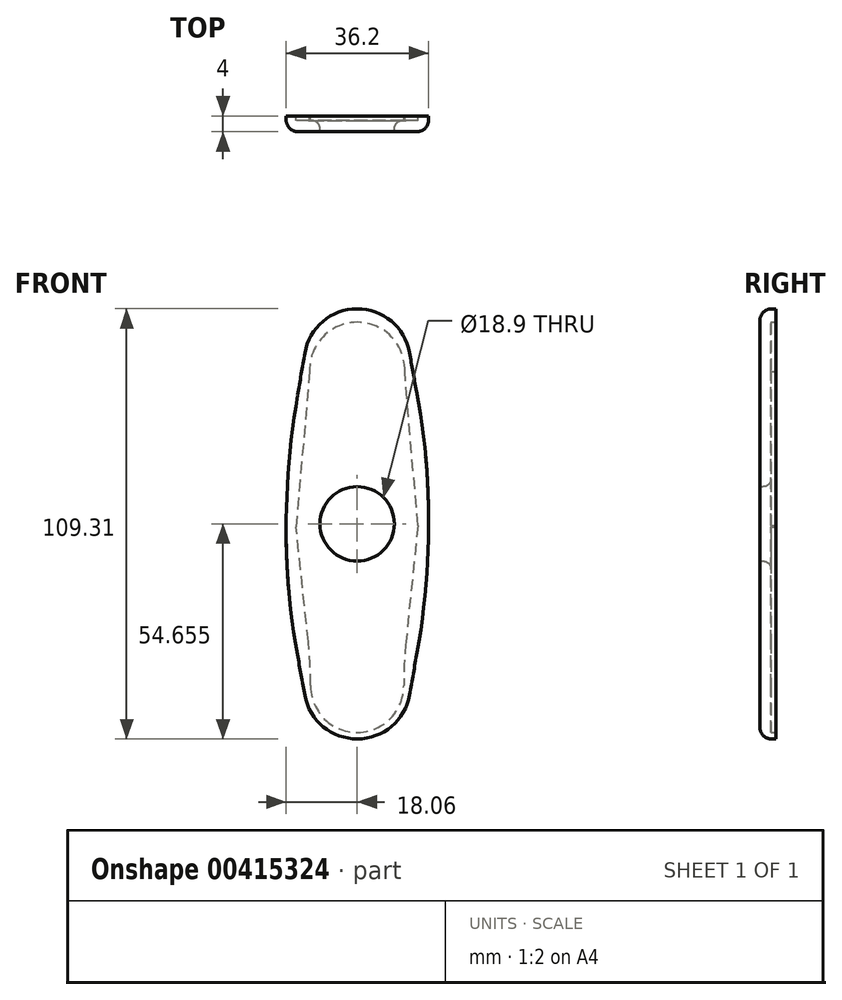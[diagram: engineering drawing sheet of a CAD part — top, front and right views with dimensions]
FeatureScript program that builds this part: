
annotation { "Feature Type Name" : "Feature", "Feature Type Description" : "" }
export const myFeature = defineFeature(function(context is Context, id is Id, definition is map)
    precondition{}
    {
        {
            var Q0;
            Q0=qCreatedBy(makeId("Front.planeOp"),FACE);
            var sketch = newSketch(context, id + "F0", { "sketchPlane" : qUnion([Q0])});
            skCircle(sketch, "E0", {"center": v(0, 60.15) * mm, "radius": 13.5 * mm});
            skCircle(sketch, "E1", {"center": v(0, -22.16) * mm, "radius": 13.5 * mm});
            skFitSpline(sketch, "E2", {"points": [v(13.5, 60.15) * mm, v(13.5, -22.16) * mm], "startDerivative": vector(18.92, -80.32) * mm, "endDerivative": vector(-18.2, -80.32) * mm});
            skFitSpline(sketch, "E3", {"points": [v(-13.5, 60.15) * mm, v(-13.5, -22.18) * mm], "startDerivative": vector(-17.3, -80.42) * mm, "endDerivative": vector(19.13, -79.67) * mm});
            skCircle(sketch, "E4", {"center": v(0, 19) * mm, "radius": 9.45 * mm});
            skCircle(sketch, "E5", {"center": v(0, 19) * mm, "radius": 11 * mm});
            skSolve(sketch);
        }
        {
            var Q0;
            Q0 = qSketchRegion(id + "F0", true);
            extrude(context, id + "F1", {"entities" : qUnion([Q0]), "depth" : 3 * mm});
        }
        {
            var Q0;
            Q0=makeQuery(id+"F1.opExtrude","SWEPT_EDGE",EDGE,{"disambiguationData":[OSD([sQuery(id+"F0.wireOp",EDGE,"E0"),sQuery(id+"F0.wireOp",EDGE,"E2")])]});
            fillet(context, id + "F2", {"entities" : qUnion([Q0]), "radius" : 802.32 * mm, "tangentPropagation" : true, "allowEdgeOverflow" : false});
        }
        {
            var Q0;
            Q0=makeQuery(id+"F1.opExtrude","SWEPT_EDGE",EDGE,{"disambiguationData":[OSD([sQuery(id+"F0.wireOp",EDGE,"E0"),sQuery(id+"F0.wireOp",EDGE,"E3")])]});
            fillet(context, id + "F3", {"entities" : qUnion([Q0]), "radius" : 4378.56 * mm, "tangentPropagation" : true, "allowEdgeOverflow" : false});
        }
        {
            var Q0;
            Q0=makeQuery(id+"F1.opExtrude","SWEPT_EDGE",EDGE,{"disambiguationData":[OSD([sQuery(id+"F0.wireOp",EDGE,"E1"),sQuery(id+"F0.wireOp",EDGE,"E2")])]});
            fillet(context, id + "F4", {"entities" : qUnion([Q0]), "radius" : 6629.57 * mm, "tangentPropagation" : true, "allowEdgeOverflow" : false});
        }
        {
            var Q0;
            Q0=makeQuery(id+"F1.opExtrude","SWEPT_EDGE",EDGE,{"disambiguationData":[OSD([sQuery(id+"F0.wireOp",EDGE,"E1"),sQuery(id+"F0.wireOp",EDGE,"E3")])]});
            fillet(context, id + "F5", {"entities" : qUnion([Q0]), "radius" : 5921.06 * mm, "tangentPropagation" : true, "allowEdgeOverflow" : false});
        }
        {
            var Q0;
            Q0=makeQuery(id+"F0.imprint","IMPRINT",FACE,{"disambiguationData":[TD([[makeQuery(id+"F0.imprint","IMPRINT",EDGE,{"derivedFrom":sQuery(id+"F0.wireOp",EDGE,"E4")}),-1.0]])]});
            extrude(context, id + "F6", {"entities" : qUnion([Q0]), "operationType" : NewBodyOperationType.ADD, "depth" : 4 * mm});
        }
        {
            var Q0;
            Q0=makeQuery(id+"F1.opExtrude","CAP_FACE",FACE,{"disambiguationData":[OSD([sQuery(id+"F0.wireOp",EDGE,"E0"),sQuery(id+"F0.wireOp",EDGE,"E1"),sQuery(id+"F0.wireOp",EDGE,"E2"),sQuery(id+"F0.wireOp",EDGE,"E3"),sQuery(id+"F0.wireOp",EDGE,"E5")])],"isStart":false});
            extrude(context, id + "F7", {"entities" : qUnion([Q0]), "operationType" : NewBodyOperationType.ADD, "depth" : 1 * mm});
        }
        {
            var Q0;
            {var subQ0=sQuery(id+"F0.wireOp",EDGE,"E5");Q0=makeQuery(id+"F6.boolean.opBoolean","MERGE",FACE,{"derivedFrom":[makeQuery(id+"F1.opExtrude","CAP_FACE",FACE,{"disambiguationData":[OSD([sQuery(id+"F0.wireOp",EDGE,"E0"),sQuery(id+"F0.wireOp",EDGE,"E1"),sQuery(id+"F0.wireOp",EDGE,"E2"),sQuery(id+"F0.wireOp",EDGE,"E3"),subQ0])],"isStart":true}),makeQuery(id+"F6.opExtrude","CAP_FACE",FACE,{"disambiguationData":[OSD([sQuery(id+"F0.wireOp",EDGE,"E4"),subQ0])],"isStart":true})]});}
            var sketch = newSketch(context, id + "F8", { "sketchPlane" : qUnion([Q0])});
            skCircle(sketch, "E6", {"center": v(0, -22.16) * mm, "radius": 11.84 * mm});
            skPoint(sketch, "E7.centerSnap0", {"position": v(0.04, 73.64) * mm});
            skLineSegment(sketch, "E8", {"start": v(11.5, -19.38) * mm, "end": v(15.54, 18.27) * mm});
            skPoint(sketch, "E8.startSnap0", {"position": v(14.24, -19.38) * mm});
            skLineSegment(sketch, "E9", {"start": v(-15.41, 18.63) * mm, "end": v(-11.5, -19.38) * mm});
            skCircle(sketch, "E10", {"center": v(0, 58.13) * mm, "radius": 12.1 * mm});
            skLineSegment(sketch, "E11", {"start": v(-15.41, 18.63) * mm, "end": v(-11.84, 60.64) * mm});
            skLineSegment(sketch, "E12", {"start": v(11.84, 60.64) * mm, "end": v(15.54, 18.27) * mm});
            skSolve(sketch);
        }
        {
            var Q0;
            Q0 = qSketchRegion(id + "F8", true);
            extrude(context, id + "F9", {"entities" : qUnion([Q0]), "operationType" : NewBodyOperationType.REMOVE, "oppositeDirection" : true, "depth" : 1.2 * mm});
        }
        {
            var Q0;
            {var subQ0=sQuery(id+"F0.wireOp",EDGE,"E5");var subQ1=sQuery(id+"F0.wireOp",EDGE,"E3");var subQ2=sQuery(id+"F0.wireOp",EDGE,"E2");var subQ3=sQuery(id+"F0.wireOp",EDGE,"E1");var subQ4=sQuery(id+"F0.wireOp",EDGE,"E0");Q0=makeQuery(id+"F7.opExtrude","CAP_EDGE",EDGE,{"disambiguationData":[OSD([subQ4,subQ3,subQ2,subQ1,subQ0]),TDD([makeQuery(id+"F2.opFillet","BLEND_EDGE",EDGE,{"blendedFrom":[makeQuery(id+"F1.opExtrude","SWEPT_EDGE",EDGE,{"disambiguationData":[OSD([subQ4,subQ2])]}),makeQuery(id+"F1.opExtrude","CAP_FACE",FACE,{"disambiguationData":[OSD([subQ4,subQ3,subQ2,subQ1,subQ0])],"isStart":false})],"blendedInto":[makeQuery(id+"F1.opExtrude","CAP_FACE",FACE,{"disambiguationData":[OSD([subQ4,subQ3,subQ2,subQ1,subQ0])],"isStart":false})]})])],"isStart":false});}
            var Q1;
            Q1=makeQuery(id+"F7.opExtrude","CAP_EDGE",EDGE,{"disambiguationData":[OSD([sQuery(id+"F0.wireOp",EDGE,"E0")])],"isStart":false});
            var Q2;
            Q2=makeQuery(id+"F7.opExtrude","CAP_EDGE",EDGE,{"disambiguationData":[OSD([sQuery(id+"F0.wireOp",EDGE,"E2")])],"isStart":false});
            var Q3;
            {var subQ0=sQuery(id+"F0.wireOp",EDGE,"E5");var subQ1=sQuery(id+"F0.wireOp",EDGE,"E3");var subQ2=sQuery(id+"F0.wireOp",EDGE,"E2");var subQ3=sQuery(id+"F0.wireOp",EDGE,"E1");var subQ4=sQuery(id+"F0.wireOp",EDGE,"E0");Q3=makeQuery(id+"F7.opExtrude","CAP_EDGE",EDGE,{"disambiguationData":[OSD([subQ4,subQ3,subQ2,subQ1,subQ0]),TDD([makeQuery(id+"F3.opFillet","BLEND_EDGE",EDGE,{"blendedFrom":[makeQuery(id+"F1.opExtrude","SWEPT_EDGE",EDGE,{"disambiguationData":[OSD([subQ4,subQ1])]}),makeQuery(id+"F1.opExtrude","CAP_FACE",FACE,{"disambiguationData":[OSD([subQ4,subQ3,subQ2,subQ1,subQ0])],"isStart":false})],"blendedInto":[makeQuery(id+"F1.opExtrude","CAP_FACE",FACE,{"disambiguationData":[OSD([subQ4,subQ3,subQ2,subQ1,subQ0])],"isStart":false})]})])],"isStart":false});}
            var Q4;
            Q4=makeQuery(id+"F7.opExtrude","CAP_EDGE",EDGE,{"disambiguationData":[OSD([sQuery(id+"F0.wireOp",EDGE,"E3")])],"isStart":false});
            var Q5;
            Q5=makeQuery(id+"F7.opExtrude","CAP_EDGE",EDGE,{"disambiguationData":[OSD([sQuery(id+"F0.wireOp",EDGE,"E1")])],"isStart":false});
            var Q6;
            {var subQ0=sQuery(id+"F0.wireOp",EDGE,"E5");var subQ1=sQuery(id+"F0.wireOp",EDGE,"E3");var subQ2=sQuery(id+"F0.wireOp",EDGE,"E2");var subQ3=sQuery(id+"F0.wireOp",EDGE,"E1");var subQ4=sQuery(id+"F0.wireOp",EDGE,"E0");Q6=makeQuery(id+"F7.opExtrude","CAP_EDGE",EDGE,{"disambiguationData":[OSD([subQ4,subQ3,subQ2,subQ1,subQ0]),TDD([makeQuery(id+"F4.opFillet","BLEND_EDGE",EDGE,{"blendedFrom":[makeQuery(id+"F1.opExtrude","SWEPT_EDGE",EDGE,{"disambiguationData":[OSD([subQ3,subQ2])]}),makeQuery(id+"F1.opExtrude","CAP_FACE",FACE,{"disambiguationData":[OSD([subQ4,subQ3,subQ2,subQ1,subQ0])],"isStart":false})],"blendedInto":[makeQuery(id+"F1.opExtrude","CAP_FACE",FACE,{"disambiguationData":[OSD([subQ4,subQ3,subQ2,subQ1,subQ0])],"isStart":false})]})])],"isStart":false});}
            var Q7;
            {var subQ0=sQuery(id+"F0.wireOp",EDGE,"E5");var subQ1=sQuery(id+"F0.wireOp",EDGE,"E3");var subQ2=sQuery(id+"F0.wireOp",EDGE,"E2");var subQ3=sQuery(id+"F0.wireOp",EDGE,"E1");var subQ4=sQuery(id+"F0.wireOp",EDGE,"E0");Q7=makeQuery(id+"F7.opExtrude","CAP_EDGE",EDGE,{"disambiguationData":[OSD([subQ4,subQ3,subQ2,subQ1,subQ0]),TDD([makeQuery(id+"F5.opFillet","BLEND_EDGE",EDGE,{"blendedFrom":[makeQuery(id+"F1.opExtrude","SWEPT_EDGE",EDGE,{"disambiguationData":[OSD([subQ3,subQ1])]}),makeQuery(id+"F1.opExtrude","CAP_FACE",FACE,{"disambiguationData":[OSD([subQ4,subQ3,subQ2,subQ1,subQ0])],"isStart":false})],"blendedInto":[makeQuery(id+"F1.opExtrude","CAP_FACE",FACE,{"disambiguationData":[OSD([subQ4,subQ3,subQ2,subQ1,subQ0])],"isStart":false})]})])],"isStart":false});}
            fillet(context, id + "F10", {"entities" : qUnion([Q0, Q1, Q2, Q3, Q4, Q5, Q6, Q7]), "radius" : 3 * mm, "tangentPropagation" : true, "allowEdgeOverflow" : false});
        }
        {
            var Q0;
            Q0=makeQuery(id+"F9.boolean.opBoolean","INTERSECT",EDGE,{"derivedFrom":[makeQuery(id+"F6.opExtrude","SWEPT_FACE",FACE,{"disambiguationData":[OSD([sQuery(id+"F0.wireOp",EDGE,"E4")])]}),makeQuery(id+"F9.opExtrude","CAP_FACE",FACE,{"disambiguationData":[OSD([sQuery(id+"F8.wireOp",EDGE,"E6"),sQuery(id+"F8.wireOp",EDGE,"E8"),sQuery(id+"F8.wireOp",EDGE,"E9"),sQuery(id+"F8.wireOp",EDGE,"E10"),sQuery(id+"F8.wireOp",EDGE,"E11"),sQuery(id+"F8.wireOp",EDGE,"E12")])],"isStart":false})]});
            fillet(context, id + "F11", {"entities" : qUnion([Q0]), "radius" : 2 * mm, "tangentPropagation" : true, "allowEdgeOverflow" : false});
        }
        {
            var Q0;
            Q0=makeQuery(id+"F9.boolean.opBoolean","COPY",EDGE,{"derivedFrom":makeQuery(id+"F9.opExtrude","SWEPT_EDGE",EDGE,{"disambiguationData":[OSD([sQuery(id+"F8.wireOp",EDGE,"E6"),sQuery(id+"F8.wireOp",EDGE,"E9")])]})});
            fillet(context, id + "F12", {"entities" : qUnion([Q0]), "radius" : 101.36 * mm, "tangentPropagation" : true, "allowEdgeOverflow" : false});
        }
        {
            var Q0;
            Q0=makeQuery(id+"F9.boolean.opBoolean","COPY",EDGE,{"derivedFrom":makeQuery(id+"F9.opExtrude","SWEPT_EDGE",EDGE,{"disambiguationData":[OSD([sQuery(id+"F8.wireOp",EDGE,"E6"),sQuery(id+"F8.wireOp",EDGE,"E8")])]})});
            fillet(context, id + "F13", {"entities" : qUnion([Q0]), "radius" : 101 * mm, "tangentPropagation" : true, "allowEdgeOverflow" : false});
        }
    });
